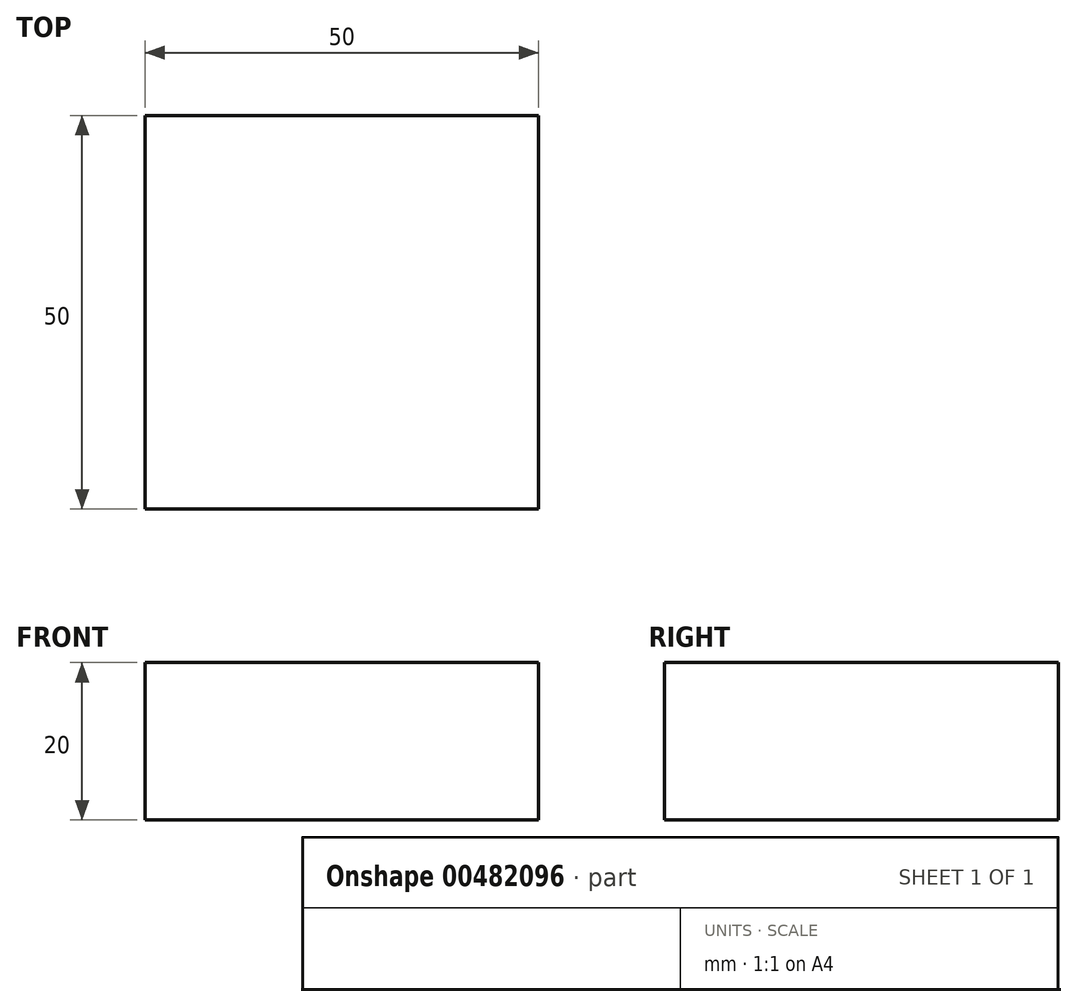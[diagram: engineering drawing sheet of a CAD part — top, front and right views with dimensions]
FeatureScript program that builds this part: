
annotation { "Feature Type Name" : "Feature", "Feature Type Description" : "" }
export const myFeature = defineFeature(function(context is Context, id is Id, definition is map)
    precondition{}
    {
        {
            var Q0;
            Q0=qCreatedBy(makeId("Front.planeOp"),FACE);
            var sketch = newSketch(context, id + "F0", { "sketchPlane" : qUnion([Q0])});
            skLineSegment(sketch, "E0.bottom", {"start": v(-30.67, 13.26) * mm, "end": v(19.33, 13.26) * mm});
            skLineSegment(sketch, "E0.top", {"start": v(-30.67, -6.74) * mm, "end": v(19.33, -6.74) * mm});
            skLineSegment(sketch, "E0.left", {"start": v(-30.67, 13.26) * mm, "end": v(-30.67, -6.74) * mm});
            skLineSegment(sketch, "E0.right", {"start": v(19.33, 13.26) * mm, "end": v(19.33, -6.74) * mm});
            skSolve(sketch);
        }
        {
            var Q0;
            Q0 = qSketchRegion(id + "F0", true);
            extrude(context, id + "F1", {"entities" : qUnion([Q0]), "depth" : 50 * mm});
        }
    });
